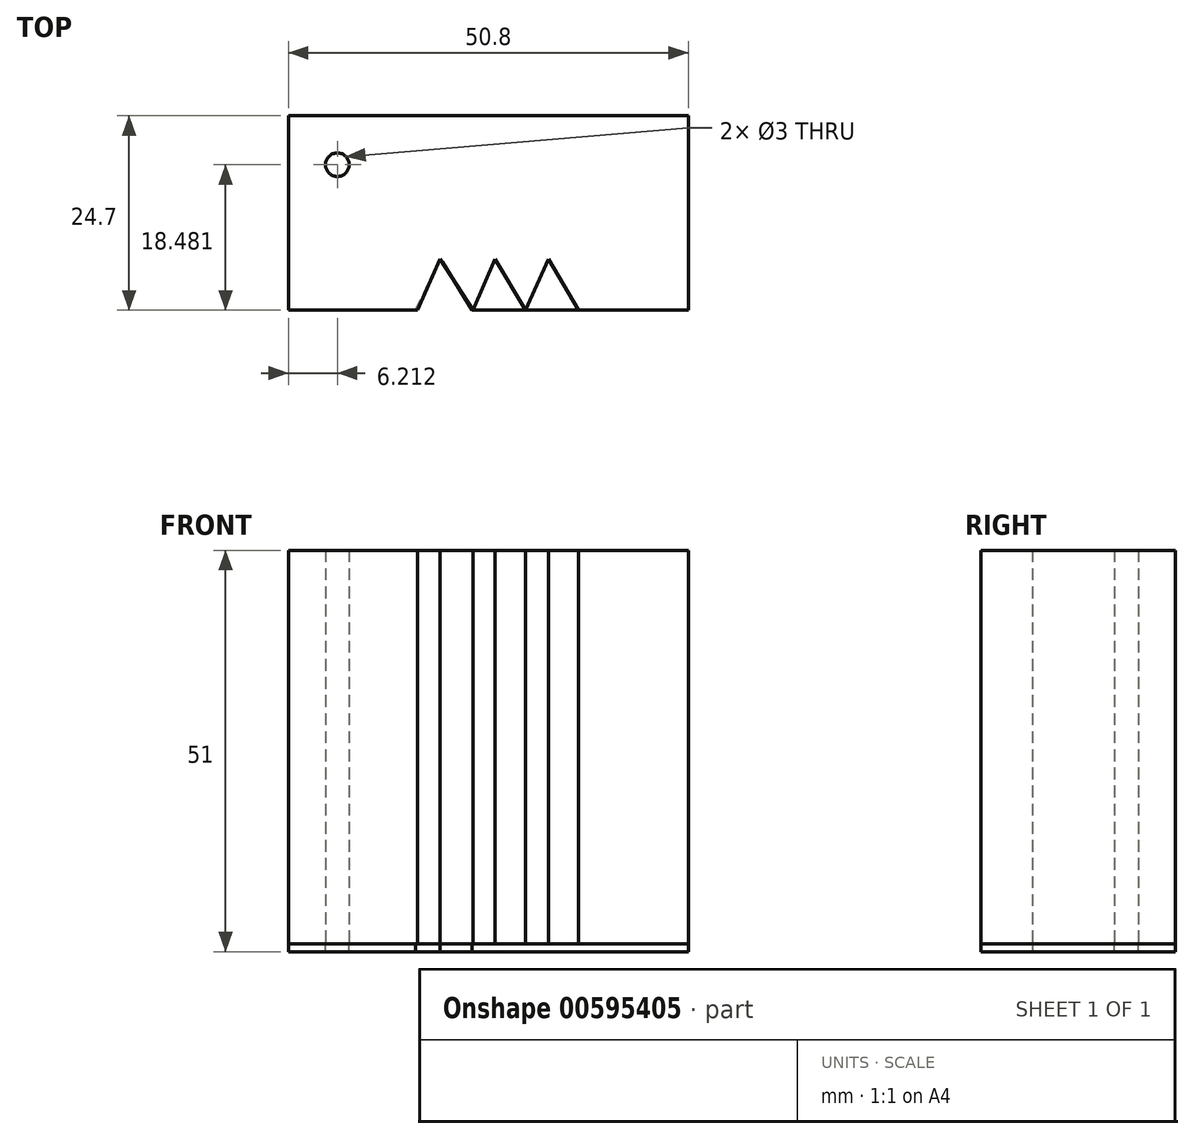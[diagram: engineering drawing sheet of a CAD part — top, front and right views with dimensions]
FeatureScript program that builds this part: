
annotation { "Feature Type Name" : "Feature", "Feature Type Description" : "" }
export const myFeature = defineFeature(function(context is Context, id is Id, definition is map)
    precondition{}
    {
        {
            var Q0;
            Q0=qCreatedBy(makeId("Top.planeOp"),FACE);
            var sketch = newSketch(context, id + "F0", { "sketchPlane" : qUnion([Q0])});
            skLineSegment(sketch, "E0.bottom", {"start": v(-25.4, 12.35) * mm, "end": v(25.4, 12.35) * mm});
            skLineSegment(sketch, "E0.top", {"start": v(-25.4, -12.35) * mm, "end": v(25.4, -12.35) * mm});
            skLineSegment(sketch, "E0.left", {"start": v(-25.4, 12.35) * mm, "end": v(-25.4, -12.35) * mm});
            skLineSegment(sketch, "E0.right", {"start": v(25.4, 12.35) * mm, "end": v(25.4, -12.35) * mm});
            skPoint(sketch, "E0.middle", {"position": v(0, 0) * mm});
            skSolve(sketch);
        }
        {
            var Q0;
            Q0 = qSketchRegion(id + "F0", true);
            extrude(context, id + "F1", {"entities" : qUnion([Q0]), "depth" : 1 * mm, "offsetDistance" : 25 * mm});
        }
        {
            var Q0;
            Q0=makeQuery(id+"F1.opExtrude","CAP_FACE",FACE,{"disambiguationData":[OSD([sQuery(id+"F0.wireOp",EDGE,"E0.bottom"),sQuery(id+"F0.wireOp",EDGE,"E0.top"),sQuery(id+"F0.wireOp",EDGE,"E0.left"),sQuery(id+"F0.wireOp",EDGE,"E0.right")])],"isStart":false});
            var sketch = newSketch(context, id + "F2", { "sketchPlane" : qUnion([Q0])});
            skCircle(sketch, "E1", {"center": v(-19.19, 6.13) * mm, "radius": 1.5 * mm});
            skSolve(sketch);
        }
        {
            var Q0;
            Q0 = qSketchRegion(id + "F2", true);
            extrude(context, id + "F3", {"entities" : qUnion([Q0]), "operationType" : NewBodyOperationType.REMOVE, "oppositeDirection" : true, "depth" : 25 * mm, "offsetDistance" : 25 * mm});
        }
        {
            var Q0;
            Q0=makeQuery(id+"F1.opExtrude","CAP_FACE",FACE,{"disambiguationData":[OSD([sQuery(id+"F0.wireOp",EDGE,"E0.bottom"),sQuery(id+"F0.wireOp",EDGE,"E0.top"),sQuery(id+"F0.wireOp",EDGE,"E0.left"),sQuery(id+"F0.wireOp",EDGE,"E0.right")])],"isStart":false});
            var sketch = newSketch(context, id + "F4", { "sketchPlane" : qUnion([Q0])});
            skLineSegment(sketch, "E2", {"start": v(-9, -12.35) * mm, "end": v(-6.12, -5.82) * mm});
            skLineSegment(sketch, "E3", {"start": v(-6.12, -5.82) * mm, "end": v(-1.94, -12.35) * mm});
            skLineSegment(sketch, "E4", {"start": v(-1.94, -12.35) * mm, "end": v(0.83, -5.82) * mm});
            skLineSegment(sketch, "E5", {"start": v(0.83, -5.82) * mm, "end": v(4.73, -12.35) * mm});
            skLineSegment(sketch, "E6", {"start": v(4.73, -12.35) * mm, "end": v(7.61, -5.82) * mm});
            skLineSegment(sketch, "E7", {"start": v(7.61, -5.82) * mm, "end": v(11.45, -12.35) * mm});
            skLineSegment(sketch, "E8", {"start": v(-9, -12.35) * mm, "end": v(0.83, -18.31) * mm});
            skLineSegment(sketch, "E9", {"start": v(11.45, -12.35) * mm, "end": v(0.83, -18.31) * mm});
            skSolve(sketch);
        }
        {
            var Q0;
            {var subQ3=sQuery(id+"F4.wireOp",EDGE,"E2");Q0=makeQuery(id+"F4.imprint","IMPRINT",FACE,{"disambiguationData":[TD([[makeQuery(id+"F4.imprint","IMPRINT",EDGE,{"derivedFrom":subQ3}),1.0]])]});}
            extrude(context, id + "F5", {"entities" : qUnion([Q0]), "depth" : 25 * mm, "offsetDistance" : 25 * mm});
        }
        {
            var Q0;
            Q0=makeQuery(id+"F5.opExtrude","CAP_FACE",FACE,{"disambiguationData":[OSD([sQuery(id+"F0.wireOp",EDGE,"E0.bottom"),sQuery(id+"F0.wireOp",EDGE,"E0.top"),sQuery(id+"F0.wireOp",EDGE,"E0.left"),sQuery(id+"F0.wireOp",EDGE,"E0.right"),sQuery(id+"F2.wireOp",EDGE,"E1"),sQuery(id+"F4.wireOp",EDGE,"E2"),sQuery(id+"F4.wireOp",EDGE,"E3"),sQuery(id+"F4.wireOp",EDGE,"E4"),sQuery(id+"F4.wireOp",EDGE,"E5"),sQuery(id+"F4.wireOp",EDGE,"E6"),sQuery(id+"F4.wireOp",EDGE,"E7")])],"isStart":false});
            extrude(context, id + "F6", {"entities" : qUnion([Q0]), "operationType" : NewBodyOperationType.ADD, "depth" : 25 * mm, "offsetDistance" : 25 * mm});
        }
        {
            var Q0;
            Q0=makeQuery(id+"F1.opExtrude","CAP_FACE",FACE,{"disambiguationData":[OSD([sQuery(id+"F0.wireOp",EDGE,"E0.bottom"),sQuery(id+"F0.wireOp",EDGE,"E0.top"),sQuery(id+"F0.wireOp",EDGE,"E0.left"),sQuery(id+"F0.wireOp",EDGE,"E0.right")])],"isStart":false});
            var sketch = newSketch(context, id + "F7", { "sketchPlane" : qUnion([Q0])});
            skLineSegment(sketch, "E10", {"start": v(-9.25, -12.35) * mm, "end": v(-6.14, -5.77) * mm});
            skLineSegment(sketch, "E11", {"start": v(-6.14, -5.77) * mm, "end": v(-2.08, -12.35) * mm});
            skLineSegment(sketch, "E12", {"start": v(-2.15, -12.28) * mm, "end": v(0.92, -5.77) * mm});
            skLineSegment(sketch, "E13", {"start": v(0.95, -5.7) * mm, "end": v(4.65, -12.35) * mm});
            skLineSegment(sketch, "E14", {"start": v(4.43, -12.5) * mm, "end": v(7.6, -5.77) * mm});
            skLineSegment(sketch, "E15", {"start": v(7.6, -5.77) * mm, "end": v(11.53, -12.35) * mm});
            skLineSegment(sketch, "E16", {"start": v(11.53, -12.35) * mm, "end": v(-9.25, -12.35) * mm});
            skSolve(sketch);
        }
        {
            var Q0;
            {var subQ0=sQuery(id+"F7.wireOp",EDGE,"E10");Q0=makeQuery(id+"F7.imprint","IMPRINT",FACE,{"disambiguationData":[TD([[makeQuery(id+"F7.imprint","IMPRINT",EDGE,{"derivedFrom":subQ0}),-1.0]])]});}
            extrude(context, id + "F8", {"entities" : qUnion([Q0]), "operationType" : NewBodyOperationType.REMOVE, "oppositeDirection" : true, "depth" : 25 * mm, "offsetDistance" : 25 * mm});
        }
    });
